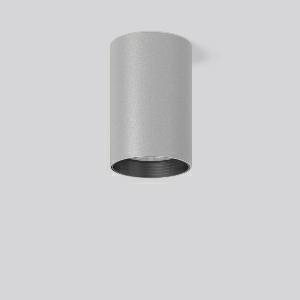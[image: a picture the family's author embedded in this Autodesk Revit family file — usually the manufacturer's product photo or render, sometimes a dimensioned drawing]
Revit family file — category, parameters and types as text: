
# Revit family: heledon_maxi_a_931250_004_2_1d16
name_source: partatom
category: Lighting Fixtures
units: mm (PartAtom-declared; Revit-internal decimal feet)

## family parameters
Cut with Voids When Loaded = No
Host = Face
Light Source = No
Part Type = Normal
Room Calculation Point = No
Round Connector Dimension = Use Diameter
Shared = No

## types (1)
- HELEDON maxi A (1 x LED Modul 927 bakery, 2900 lm, 2700)
    Apparent Load = 33 VA
    Approval mark = CE
    CIE Flux Codes = 96 99 100 100 100
    Color Rendering = 90
    Color Temperature = 2700
    Default Elevation = 1800 mm
    Description = Series: HELEDON maxi
Cylindrical surface-mounted downlight. Housing: die-cast aluminium, powder-coated. Internal ceiling frame polycarbonate with bayonet mounting. Black plastic ring and recessed LED to prevent glare from the side. Optical assembly with lens made of plastic (polycarbonate) for the best homogeneous light distribution - can be changed without tools. Special LED for illumination of pastries included. Suitable for Ceiling mounting. Easy installation with a separate ceiling frame with bayonet mounting and plug connection. Driver integrated. Connected via plug-in connector. High quality converter without flickering and stroboscopic effect. The following accessories can be mounted without use of tools: interchangeable lenses, decorative glasses, honeycomb louvre, clear and frosted diffusers, white interchangeable plastic ring. 
Colour: silver
Diameter: 123 mm
Height: 183 mm
Lamp: LED
Socket: without socket
Colour temperature: bakery
Colour rendering index (CRI): 97
System power: 33 W
Rated luminous flux: 2900 lm
Luminous efficiency: 88 lm/W
Control gear: Regulated power supply
Protection class: I
Type of protection: IP 20
    Height = 183 mm
    Lamp = 1 x LED Modul 927 bakery
    Lamp Light Flux = 2900 lm
    Lamp count = 1
    Length = 123 mm
    Lifetime = 50000 h
    Luminous efficacy = 88 lm/W
    Manufacturer = RZB
    ModVariant = No
    Model = 931250.004.2
    Mounting Place = Ceiling
    Mounting Type = Surface mounted
    Number of Poles = 1
    OnlyDefault = Yes
    Power Factor = 1
    Product Name = HELEDON maxi A
    Product group = Surface mounted downlights
    ProductGroupID = 302
    Protection Class = Protection class I
    Protection Degree = IP 20
    RLX_Detail_Level = 1
    RLX_Emergency_Light_Flux = 0 lm
    RLX_Emergency_Type = 0
    RLX_Emergency_Type_DB = No
    RlxData = <blob elided: 97781 chars, md5=6c3a777a>
    Socket = socket
    Standby Power = 0 W
    System Light Flux = 2900 lm
    System Power = 33 W
    Type Comments = Product without accessories
    Type Image = 931193.004.jpg
    URL = http://relux.com
    VarID = ---
    Voltage = 230 V
    Voltage Range = 220-240 V
    Weight = 0.00 kg
    Width = 0 mm  [stored 0 ft]

note: [stored X ft] marks values corroborated as IEEE doubles in the binary element streams (Revit-internal decimal feet)

## geometry (parser evidence)
native form markers: Blend x4, Sweep x10
no freeform markers — native parametric forms only
